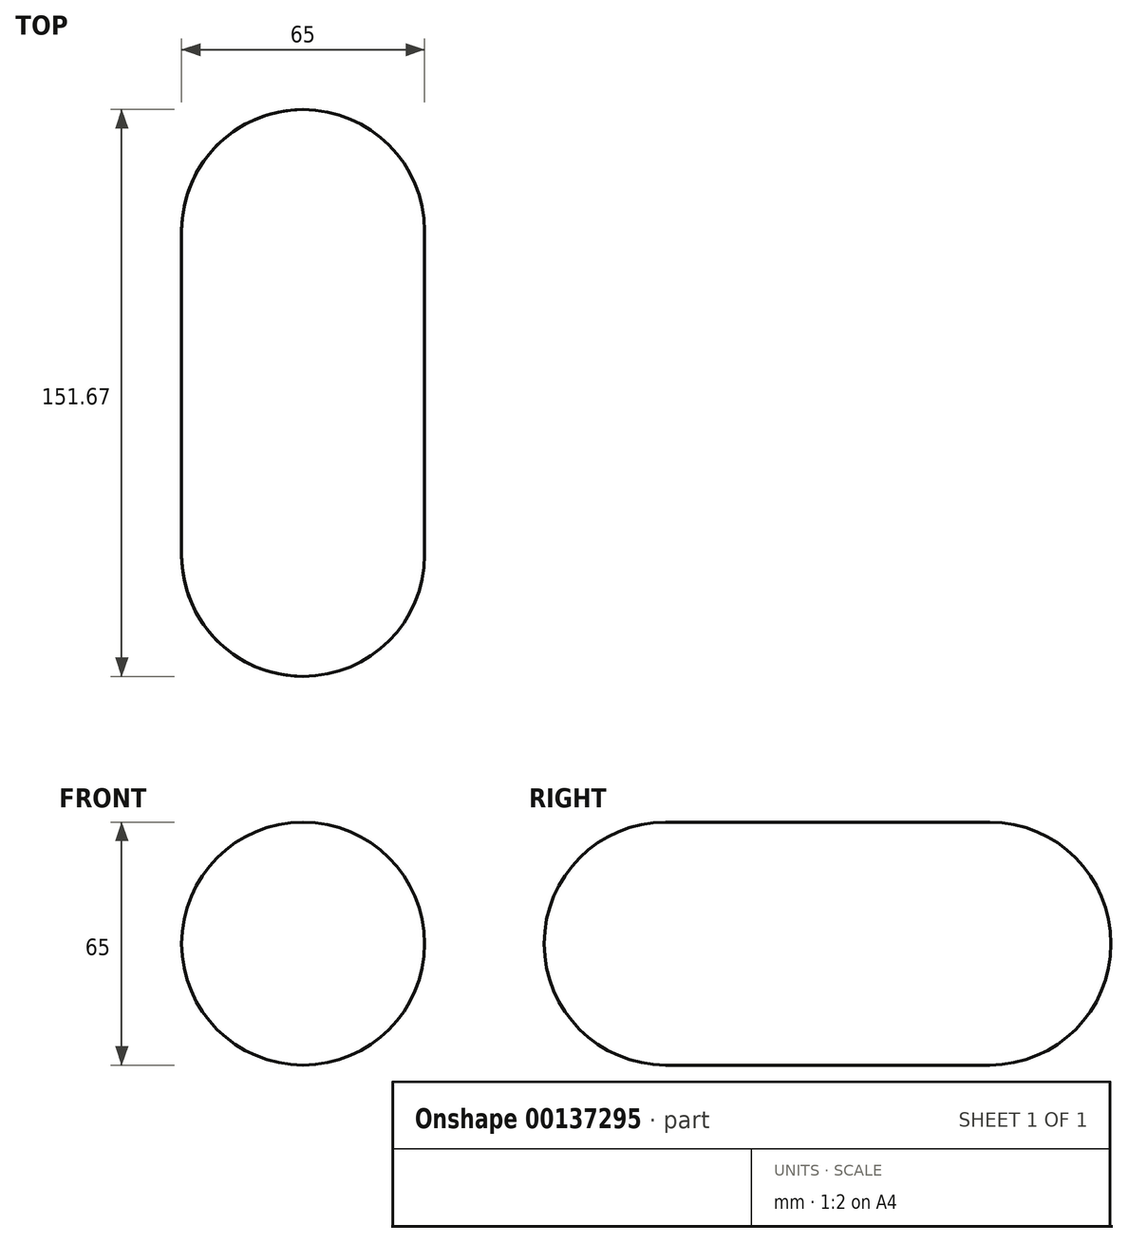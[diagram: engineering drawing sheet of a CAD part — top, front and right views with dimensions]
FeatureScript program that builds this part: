
annotation { "Feature Type Name" : "Feature", "Feature Type Description" : "" }
export const myFeature = defineFeature(function(context is Context, id is Id, definition is map)
    precondition{}
    {
        {
            var Q0;
            Q0=qCreatedBy(makeId("Top.planeOp"),FACE);
            var sketch = newSketch(context, id + "F0", { "sketchPlane" : qUnion([Q0])});
            skArc(sketch, "E0", {"start": v(0, 0) * mm, "mid": v(9.52, -22.98) * mm, "end": v(32.5, -32.5) * mm});
            skLineSegment(sketch, "E1", {"start": v(0, 0) * mm, "end": v(32.5, 0) * mm, "construction": true});
            skLineSegment(sketch, "E2", {"start": v(0, 0) * mm, "end": v(0, 86.67) * mm});
            skArc(sketch, "E3", {"start": v(0, 86.67) * mm, "mid": v(9.52, 109.65) * mm, "end": v(32.5, 119.17) * mm});
            skLineSegment(sketch, "E4", {"start": v(0, 43.33) * mm, "end": v(65, 43.33) * mm, "construction": true});
            skLineSegment(sketch, "E5", {"start": v(0, 86.67) * mm, "end": v(32.5, 86.67) * mm, "construction": true});
            skLineSegment(sketch, "E6", {"start": v(32.5, -32.5) * mm, "end": v(32.5, 119.17) * mm});
            skArc(sketch, "E7", {"start": v(65, -0.23) * mm, "mid": v(65, -0.11) * mm, "end": v(65, 0) * mm});
            skSolve(sketch);
        }
        {
            var Q0;
            Q0=makeQuery(id+"F0.imprint","IMPRINT",FACE,{"disambiguationData":[TD([[makeQuery(id+"F0.imprint","IMPRINT",EDGE,{"derivedFrom":sQuery(id+"F0.wireOp",EDGE,"E0")}),1.0]])]});
            var Q1;
            Q1=sQuery(id+"F0.wireOp",EDGE,"E6");
            revolve(context, id + "F1", {"entities" : qUnion([Q0]), "axis" : qUnion([Q1]), "revolveType" : RevolveType.FULL});
        }
    });
